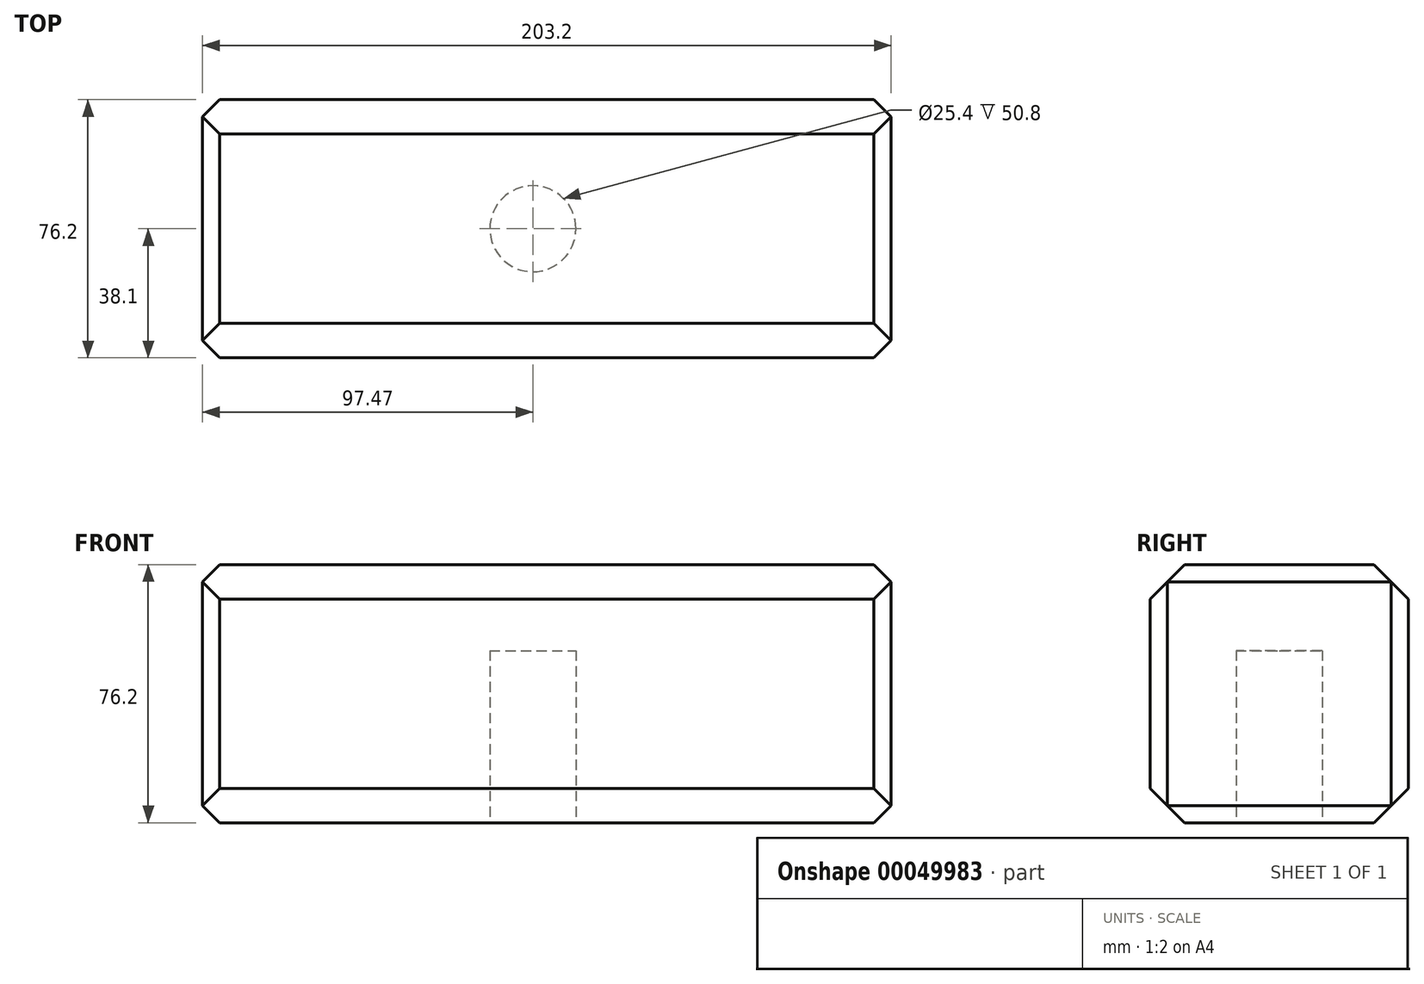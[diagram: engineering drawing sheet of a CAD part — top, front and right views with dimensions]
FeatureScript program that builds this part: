
annotation { "Feature Type Name" : "Feature", "Feature Type Description" : "" }
export const myFeature = defineFeature(function(context is Context, id is Id, definition is map)
    precondition{}
    {
        {
            var Q0;
            Q0=qCreatedBy(makeId("Front.planeOp"),FACE);
            var sketch = newSketch(context, id + "F0", { "sketchPlane" : qUnion([Q0])});
            skLineSegment(sketch, "E0.bottom", {"start": v(-97.47, 28.28) * mm, "end": v(105.73, 28.28) * mm});
            skLineSegment(sketch, "E0.top", {"start": v(-97.47, -47.92) * mm, "end": v(105.73, -47.92) * mm});
            skLineSegment(sketch, "E0.left", {"start": v(-97.47, 28.28) * mm, "end": v(-97.47, -47.92) * mm});
            skLineSegment(sketch, "E0.right", {"start": v(105.73, 28.28) * mm, "end": v(105.73, -47.92) * mm});
            skSolve(sketch);
        }
        {
            var Q0;
            Q0 = qSketchRegion(id + "F0", true);
            extrude(context, id + "F1", {"entities" : qUnion([Q0]), "depth" : 76.2 * mm});
        }
        {
            var Q0;
            Q0=makeQuery(id+"F1.opExtrude","CAP_EDGE",EDGE,{"disambiguationData":[OSD([sQuery(id+"F0.wireOp",EDGE,"E0.bottom")])],"isStart":false});
            var Q1;
            Q1=makeQuery(id+"F1.opExtrude","CAP_EDGE",EDGE,{"disambiguationData":[OSD([sQuery(id+"F0.wireOp",EDGE,"E0.top")])],"isStart":false});
            var Q2;
            Q2=makeQuery(id+"F1.opExtrude","CAP_EDGE",EDGE,{"disambiguationData":[OSD([sQuery(id+"F0.wireOp",EDGE,"E0.bottom")])],"isStart":true});
            var Q3;
            Q3=makeQuery(id+"F1.opExtrude","CAP_EDGE",EDGE,{"disambiguationData":[OSD([sQuery(id+"F0.wireOp",EDGE,"E0.top")])],"isStart":true});
            chamfer(context, id + "F2", {"entities" : qUnion([Q0, Q1, Q2, Q3]), "width" : 10.16 * mm, "tangentPropagation" : true});
        }
        {
            var Q0;
            Q0=makeQuery(id+"F1.opExtrude","SWEPT_EDGE",EDGE,{"disambiguationData":[OSD([sQuery(id+"F0.wireOp",EDGE,"E0.bottom"),sQuery(id+"F0.wireOp",EDGE,"E0.left")])]});
            var Q1;
            Q1=makeQuery(id+"F1.opExtrude","CAP_EDGE",EDGE,{"disambiguationData":[OSD([sQuery(id+"F0.wireOp",EDGE,"E0.left")])],"isStart":false});
            var Q2;
            Q2=makeQuery(id+"F1.opExtrude","SWEPT_EDGE",EDGE,{"disambiguationData":[OSD([sQuery(id+"F0.wireOp",EDGE,"E0.top"),sQuery(id+"F0.wireOp",EDGE,"E0.left")])]});
            var Q3;
            Q3=makeQuery(id+"F1.opExtrude","CAP_EDGE",EDGE,{"disambiguationData":[OSD([sQuery(id+"F0.wireOp",EDGE,"E0.left")])],"isStart":true});
            var Q4;
            Q4=makeQuery(id+"F1.opExtrude","CAP_EDGE",EDGE,{"disambiguationData":[OSD([sQuery(id+"F0.wireOp",EDGE,"E0.right")])],"isStart":true});
            var Q5;
            Q5=makeQuery(id+"F1.opExtrude","SWEPT_EDGE",EDGE,{"disambiguationData":[OSD([sQuery(id+"F0.wireOp",EDGE,"E0.top"),sQuery(id+"F0.wireOp",EDGE,"E0.right")])]});
            var Q6;
            Q6=makeQuery(id+"F1.opExtrude","CAP_EDGE",EDGE,{"disambiguationData":[OSD([sQuery(id+"F0.wireOp",EDGE,"E0.right")])],"isStart":false});
            var Q7;
            Q7=makeQuery(id+"F1.opExtrude","SWEPT_EDGE",EDGE,{"disambiguationData":[OSD([sQuery(id+"F0.wireOp",EDGE,"E0.bottom"),sQuery(id+"F0.wireOp",EDGE,"E0.right")])]});
            chamfer(context, id + "F3", {"entities" : qUnion([Q0, Q1, Q2, Q3, Q4, Q5, Q6, Q7]), "width" : 5.08 * mm, "tangentPropagation" : true});
        }
        {
            var Q0;
            Q0=makeQuery(id+"F1.opExtrude","SWEPT_FACE",FACE,{"disambiguationData":[OSD([sQuery(id+"F0.wireOp",EDGE,"E0.top")])]});
            var sketch = newSketch(context, id + "F4", { "sketchPlane" : qUnion([Q0])});
            skCircle(sketch, "E1", {"center": v(0, 38.1) * mm, "radius": 12.7 * mm});
            skPoint(sketch, "E1.centerSnap0", {"position": v(-92.4, 38.1) * mm});
            skSolve(sketch);
        }
        {
            var Q0;
            Q0 = qSketchRegion(id + "F4", true);
            extrude(context, id + "F5", {"entities" : qUnion([Q0]), "operationType" : NewBodyOperationType.REMOVE, "oppositeDirection" : true, "depth" : 50.8 * mm});
        }
    });
